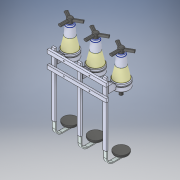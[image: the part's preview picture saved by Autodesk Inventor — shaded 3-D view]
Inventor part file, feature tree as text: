
AUTODESK INVENTOR PART (.ipt)
format: ipt  version: 2017 (Build 210142000, 142)  size: 592,896 bytes
history: mixed  units: mm
features: other x6, mirror x3, fillet x2, revolve x1, imported_body x1
ambient origin geometry x8: Origin, YZ Plane, XZ Plane, XY Plane, X Axis, Y Axis, Z Axis, Center Point
bodies: Solid1 (imported_parasolid), Solid2 (imported_parasolid), Solid3 (imported_parasolid), Solid4 (imported_parasolid), Solid5 (imported_parasolid), Solid6 (imported_parasolid), Solid7 (imported_parasolid), Solid8 (imported_parasolid), Solid9 (imported_parasolid), Solid10 (imported_parasolid), Solid11 (imported_parasolid), Solid12 (imported_parasolid)
feature tree (13):
  revolve  "Revolve1"  [1 undecoded]
  fillet  "Fillet4"  [1 undecoded]
  fillet  "Fillet6"  [1 undecoded]
  other  "LPattern12[1]"
  other  "LPattern12[2]"
  other  "LPattern12[3]"
  mirror  "Mirror2[1]"
  mirror  "Mirror2[2]"
  mirror  "Mirror2[3]"
  other  "LPattern13[1]"
  other  "LPattern13[2]"
  other  "LPattern13[3]"
  imported_body  NMx_Import_Brep_tag  [imported B-rep: ~45 faces, bbox_mm=None]
note: 3 required parameter values undecoded (feature->parameter linkage not recoverable at this tier; creation-order binding heuristic only, values carry confidence <= 0.55)
